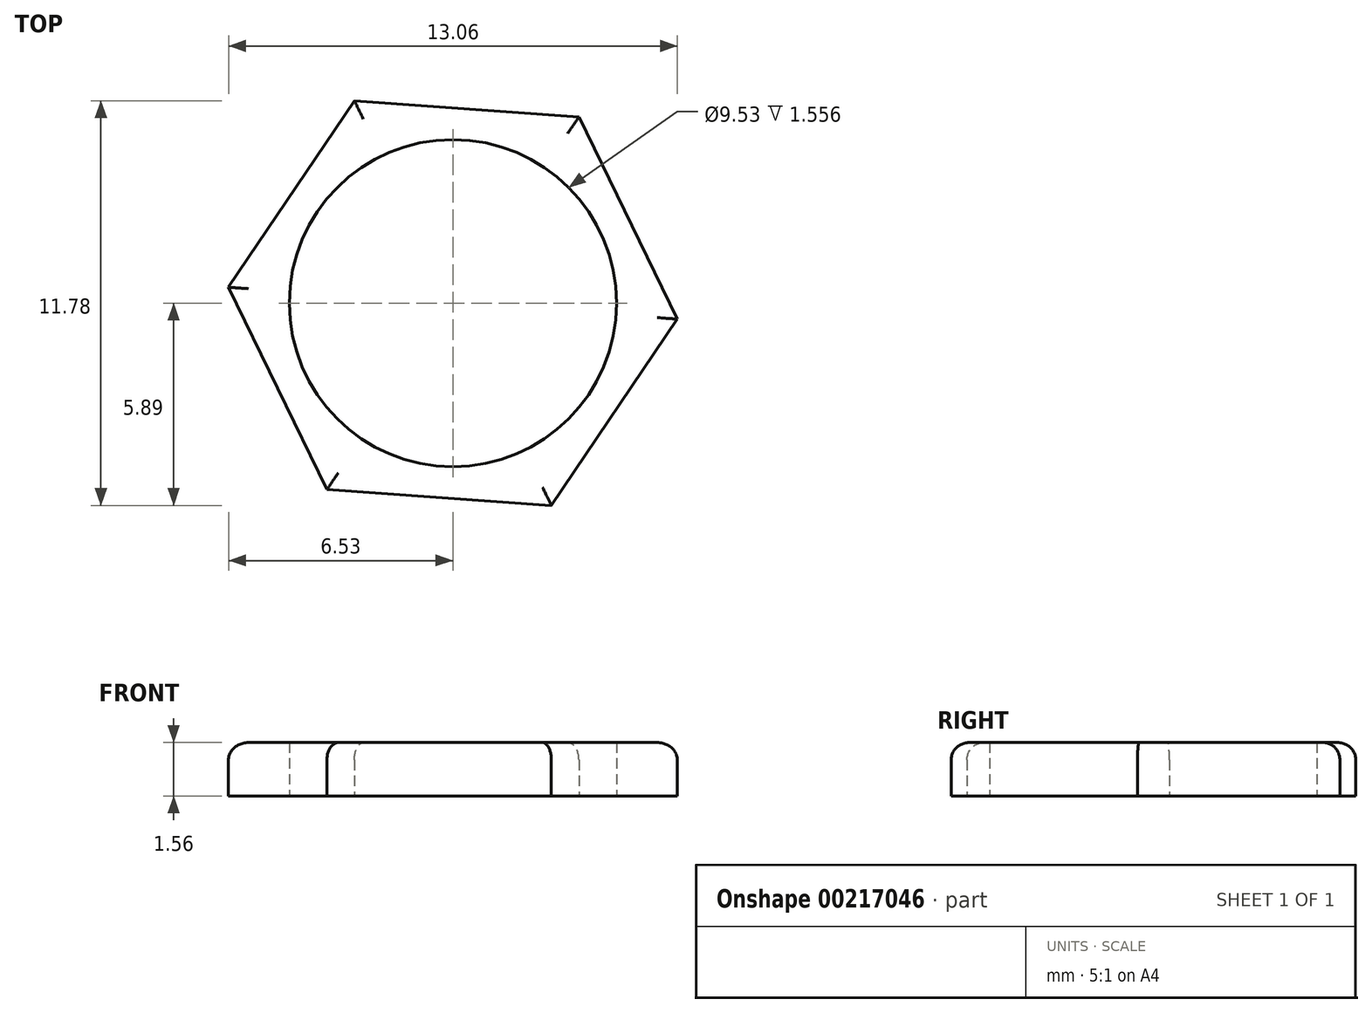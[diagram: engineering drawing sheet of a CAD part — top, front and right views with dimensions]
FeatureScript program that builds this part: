
annotation { "Feature Type Name" : "Feature", "Feature Type Description" : "" }
export const myFeature = defineFeature(function(context is Context, id is Id, definition is map)
    precondition{}
    {
        {
            var Q0;
            Q0=qCreatedBy(makeId("Top.planeOp"),FACE);
            var sketch = newSketch(context, id + "F0", { "sketchPlane" : qUnion([Q0])});
            skCircle(sketch, "E0", {"center": v(0, 0) * mm, "radius": 4.76 * mm});
            skLineSegment(sketch, "E1.0", {"start": v(6.53, -0.46) * mm, "end": v(2.87, -5.89) * mm});
            skLineSegment(sketch, "E1.1", {"start": v(2.87, -5.89) * mm, "end": v(-3.67, -5.43) * mm});
            skLineSegment(sketch, "E1.2", {"start": v(-3.67, -5.43) * mm, "end": v(-6.53, 0.46) * mm});
            skLineSegment(sketch, "E1.3", {"start": v(-6.53, 0.46) * mm, "end": v(-2.87, 5.89) * mm});
            skLineSegment(sketch, "E1.4", {"start": v(-2.87, 5.89) * mm, "end": v(3.67, 5.43) * mm});
            skLineSegment(sketch, "E1.5", {"start": v(3.67, 5.43) * mm, "end": v(6.53, -0.46) * mm});
            skPoint(sketch, "E1.0.midPoint", {"position": v(4.7, -3.18) * mm});
            skSolve(sketch);
        }
        {
            var Q0;
            Q0=makeQuery(id+"F0.imprint","IMPRINT",FACE,{"disambiguationData":[TD([[makeQuery(id+"F0.imprint","IMPRINT",EDGE,{"derivedFrom":sQuery(id+"F0.wireOp",EDGE,"E0")}),-1.0]])]});
            extrude(context, id + "F1", {"entities" : qUnion([Q0]), "depth" : 1.56 * mm});
        }
        {
            var Q0;
            Q0=makeQuery(id+"F1.opExtrude","CAP_EDGE",EDGE,{"disambiguationData":[OSD([sQuery(id+"F0.wireOp",EDGE,"E1.2")])],"isStart":false});
            var Q1;
            Q1=makeQuery(id+"F1.opExtrude","CAP_EDGE",EDGE,{"disambiguationData":[OSD([sQuery(id+"F0.wireOp",EDGE,"E1.1")])],"isStart":false});
            var Q2;
            Q2=makeQuery(id+"F1.opExtrude","CAP_EDGE",EDGE,{"disambiguationData":[OSD([sQuery(id+"F0.wireOp",EDGE,"E1.0")])],"isStart":false});
            var Q3;
            Q3=makeQuery(id+"F1.opExtrude","CAP_EDGE",EDGE,{"disambiguationData":[OSD([sQuery(id+"F0.wireOp",EDGE,"E1.5")])],"isStart":false});
            var Q4;
            Q4=makeQuery(id+"F1.opExtrude","CAP_EDGE",EDGE,{"disambiguationData":[OSD([sQuery(id+"F0.wireOp",EDGE,"E1.4")])],"isStart":false});
            var Q5;
            Q5=makeQuery(id+"F1.opExtrude","CAP_EDGE",EDGE,{"disambiguationData":[OSD([sQuery(id+"F0.wireOp",EDGE,"E1.3")])],"isStart":false});
            fillet(context, id + "F2", {"entities" : qUnion([Q0, Q1, Q2, Q3, Q4, Q5]), "radius" : 0.5 * mm, "tangentPropagation" : true, "allowEdgeOverflow" : false});
        }
    });
